# Revit family: LEGRAND_NON INTERLOCKED SOCKETS_SURFACE MOUNTED_IP44_230_SYMBOL
name_source: partatom
category: Annotations génériques
revit_build: Autodesk Revit 2018 (Build: 20170223_1515(x64)
units: mm (PartAtom-declared; Revit-internal decimal feet)

## family parameters
Conserve la lisibilité du texte = Non
Partagée = Non
Rotation avec le composant = Non

## types (17) — shared parameters
diameter symbol = 10 mm  [stored 0.0328084 ft]
interlocked sockets = Non
lock radius = 0.8 mm  [stored 0.00262467 ft]
pole radius = 1 mm  [stored 0.00328084 ft]
radius symbol = 5 mm  [stored 0.0164042 ft]

## per-type parameters (varying)
| type | 2P+H | 3P+H | 3P+H+N |
| Symbol ref.052018 | Non | Oui | Non |
| Symbol ref.052019 | Non | Oui | Non |
| Symbol ref.052020 | Non | Non | Oui |
| Symbol ref.052022 | Non | Oui | Non |
| Symbol ref.052023 | Non | Oui | Non |
| Symbol ref.052024 | Non | Non | Oui |
| Symbol ref.052032 | Non | Oui | Non |
| Symbol ref.052033 | Non | Oui | Non |
| Symbol ref.052034 | Non | Non | Oui |
| Symbol ref.052718 | Non | Oui | Non |
| Symbol ref.052719 | Non | Oui | Non |
| Symbol ref.052720 | Non | Non | Oui |
| Symbol ref.052732 | Non | Non | Oui |
| Symbol ref.052733 | Non | Oui | Non |
| Symbol ref.053622 | Oui | Non | Non |
| Symbol ref.053623 | Non | Oui | Non |
| Symbol ref.053903 | Oui | Non | Non |

note: [stored X ft] marks values corroborated as IEEE doubles in the binary element streams (Revit-internal decimal feet)
